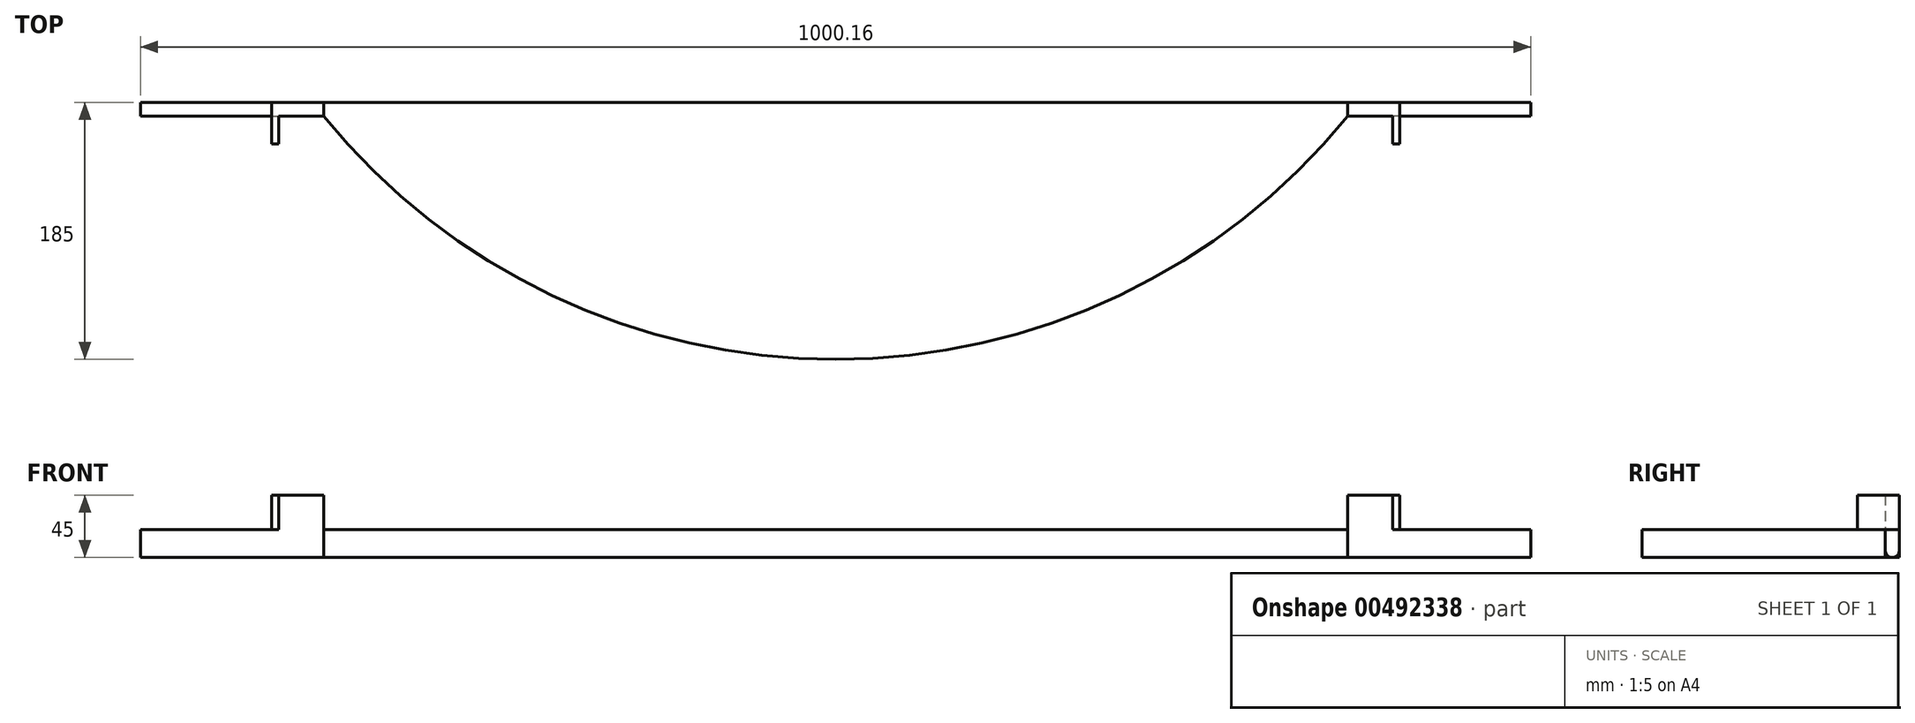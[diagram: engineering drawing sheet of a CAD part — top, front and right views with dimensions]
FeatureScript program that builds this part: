
annotation { "Feature Type Name" : "Feature", "Feature Type Description" : "" }
export const myFeature = defineFeature(function(context is Context, id is Id, definition is map)
    precondition{}
    {
        {
            var Q0;
            Q0=qCreatedBy(makeId("Top.planeOp"),FACE);
            var sketch = newSketch(context, id + "F0", { "sketchPlane" : qUnion([Q0])});
            skArc(sketch, "E0", {"start": v(-368.27, -300) * mm, "mid": v(0, -475) * mm, "end": v(368.27, -300) * mm});
            skLineSegment(sketch, "E1", {"start": v(-368.27, -300) * mm, "end": v(-368.27, -290) * mm});
            skLineSegment(sketch, "E2", {"start": v(-368.27, -290) * mm, "end": v(368.27, -290) * mm});
            skLineSegment(sketch, "E3", {"start": v(368.27, -290) * mm, "end": v(368.27, -300) * mm});
            skSolve(sketch);
        }
        {
            var Q0;
            Q0 = qSketchRegion(id + "F0", true);
            extrude(context, id + "F1", {"entities" : qUnion([Q0]), "depth" : 20 * mm});
        }
        {
            var Q0;
            Q0=makeQuery(id+"F1.opExtrude","SWEPT_FACE",FACE,{"disambiguationData":[OSD([sQuery(id+"F0.wireOp",EDGE,"E3")])]});
            var sketch = newSketch(context, id + "F2", { "sketchPlane" : qUnion([Q0])});
            skArc(sketch, "E4", {"start": v(-300, 5) * mm, "mid": v(-295, 0) * mm, "end": v(-290, 5) * mm});
            skLineSegment(sketch, "E5", {"start": v(-300, 5) * mm, "end": v(-300, 20) * mm});
            skLineSegment(sketch, "E6", {"start": v(-300, 20) * mm, "end": v(-290, 20) * mm});
            skLineSegment(sketch, "E7", {"start": v(-290, 20) * mm, "end": v(-290, 5) * mm});
            skSolve(sketch);
        }
        {
            var Q0;
            Q0 = qSketchRegion(id + "F2", true);
            extrude(context, id + "F3", {"entities" : qUnion([Q0]), "operationType" : NewBodyOperationType.ADD, "depth" : 131.8 * mm});
        }
        {
            var Q0;
            Q0=makeQuery(id+"F1.opExtrude","SWEPT_FACE",FACE,{"disambiguationData":[OSD([sQuery(id+"F0.wireOp",EDGE,"E1")])]});
            var sketch = newSketch(context, id + "F4", { "sketchPlane" : qUnion([Q0])});
            skLineSegment(sketch, "E8", {"start": v(290, 5) * mm, "end": v(290, 20) * mm});
            skLineSegment(sketch, "E9", {"start": v(290, 20) * mm, "end": v(300, 20) * mm});
            skLineSegment(sketch, "E10", {"start": v(300, 20) * mm, "end": v(300, 5) * mm});
            skArc(sketch, "E11", {"start": v(290, 5) * mm, "mid": v(295, 0) * mm, "end": v(300, 5) * mm});
            skSolve(sketch);
        }
        {
            var Q0;
            {var subQ1=sQuery(id+"F4.wireOp",EDGE,"E8");Q0=makeQuery(id+"F4.imprint","IMPRINT",FACE,{"disambiguationData":[TD([[makeQuery(id+"F4.imprint","IMPRINT",EDGE,{"derivedFrom":subQ1}),1.0]])]});}
            extrude(context, id + "F5", {"entities" : qUnion([Q0]), "operationType" : NewBodyOperationType.ADD, "depth" : 131.8 * mm});
        }
        {
            var Q0;
            Q0=makeQuery(id+"F5.boolean.opBoolean","MERGE",FACE,{"derivedFrom":[makeQuery(id+"F3.boolean.opBoolean","MERGE",FACE,{"derivedFrom":[makeQuery(id+"F1.opExtrude","CAP_FACE",FACE,{"disambiguationData":[OSD([sQuery(id+"F0.wireOp",EDGE,"E0"),sQuery(id+"F0.wireOp",EDGE,"E1"),sQuery(id+"F0.wireOp",EDGE,"E2"),sQuery(id+"F0.wireOp",EDGE,"E3")])],"isStart":false}),makeQuery(id+"F3.opExtrude","SWEPT_FACE",FACE,{"disambiguationData":[OSD([sQuery(id+"F2.wireOp",EDGE,"E6")])]})]}),makeQuery(id+"F5.opExtrude","SWEPT_FACE",FACE,{"disambiguationData":[OSD([sQuery(id+"F4.wireOp",EDGE,"E9")])]})]});
            var sketch = newSketch(context, id + "F6", { "sketchPlane" : qUnion([Q0])});
            skLineSegment(sketch, "E12", {"start": v(-405.77, -290) * mm, "end": v(-405.77, -320) * mm});
            skLineSegment(sketch, "E13", {"start": v(-405.77, -320) * mm, "end": v(-400.77, -320) * mm});
            skLineSegment(sketch, "E14", {"start": v(-400.77, -320) * mm, "end": v(-400.77, -300) * mm});
            skLineSegment(sketch, "E15", {"start": v(-400.77, -300) * mm, "end": v(-368.27, -300) * mm});
            skLineSegment(sketch, "E16", {"start": v(-368.27, -290) * mm, "end": v(-405.77, -290) * mm});
            skLineSegment(sketch, "E17", {"start": v(400.77, -300) * mm, "end": v(400.77, -320) * mm});
            skLineSegment(sketch, "E18", {"start": v(400.77, -320) * mm, "end": v(405.77, -320) * mm});
            skLineSegment(sketch, "E19", {"start": v(405.77, -320) * mm, "end": v(405.77, -290) * mm});
            skLineSegment(sketch, "E20", {"start": v(-368.27, -300) * mm, "end": v(-368.27, -290) * mm});
            skLineSegment(sketch, "E21", {"start": v(368.27, -300) * mm, "end": v(400.77, -300) * mm});
            skLineSegment(sketch, "E22", {"start": v(368.27, -300) * mm, "end": v(368.27, -290) * mm});
            skLineSegment(sketch, "E23", {"start": v(368.27, -290) * mm, "end": v(405.77, -290) * mm});
            skSolve(sketch);
        }
        {
            var Q0;
            Q0=makeQuery(id+"F6.imprint","IMPRINT",FACE,{"disambiguationData":[TD([[makeQuery(id+"F6.imprint","IMPRINT",EDGE,{"derivedFrom":sQuery(id+"F6.wireOp",EDGE,"E20")}),1.0]])]});
            var Q1;
            {var subQ0=sQuery(id+"F6.wireOp",EDGE,"E13");Q1=makeQuery(id+"F6.imprint","IMPRINT",FACE,{"disambiguationData":[TD([[makeQuery(id+"F6.imprint","IMPRINT",EDGE,{"derivedFrom":subQ0}),1.0]])]});}
            var Q2;
            {var subQ1=sQuery(id+"F6.wireOp",EDGE,"E21");Q2=makeQuery(id+"F6.imprint","IMPRINT",FACE,{"disambiguationData":[TD([[makeQuery(id+"F6.imprint","IMPRINT",EDGE,{"derivedFrom":subQ1}),-1.0]])]});}
            var Q3;
            {var subQ0=sQuery(id+"F6.wireOp",EDGE,"E17");Q3=makeQuery(id+"F6.imprint","IMPRINT",FACE,{"disambiguationData":[TD([[makeQuery(id+"F6.imprint","IMPRINT",EDGE,{"derivedFrom":subQ0}),1.0]])]});}
            extrude(context, id + "F7", {"entities" : qUnion([Q0, Q1, Q2, Q3]), "operationType" : NewBodyOperationType.ADD, "depth" : 25 * mm});
        }
    });
